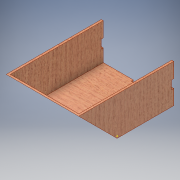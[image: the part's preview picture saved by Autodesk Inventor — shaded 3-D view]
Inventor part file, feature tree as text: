
AUTODESK INVENTOR PART (.ipt)
format: ipt  version: 2017 (Build 210142000, 142)  size: 214,528 bytes
history: native  units: in
note: dims shown in document units (in); Inventor stores cm internally (conversion verified against a paired STEP export)
features: sketch x10, extrude x9, fillet x1
ambient origin geometry x8: Origin, YZ Plane, XZ Plane, XY Plane, X Axis, Y Axis, Z Axis, Center Point
bodies: Solid1 (feature_tree)
feature tree (20):
  extrude  "Extrusion1"  Depth=0.1875in TaperAngle=0.0deg
  sketch  "Sketch2"  dims[d4=0.1875in d5=0.1875in]
  extrude  "Extrusion2"  Depth=0.1875in
  sketch  "Sketch3"  dims[d6=3.3558in d7=0.0in d8=4.7244in]
  sketch  "Sketch4"  dims[d9=45.0deg d11=45.0deg]
  extrude  "Extrusion3"  Depth=3.3558in
  extrude  "Extrusion4"  TaperAngle=45.0deg  [1 undecoded]
  extrude  "Extrusion5"  Depth=3.9557in TaperAngle=0.0deg
  extrude  "Extrusion6"  Depth=3.3558in TaperAngle=0.0deg
  extrude  "Extrusion7"  Depth=6.6929in
  extrude  "Extrusion8"  Depth=2.9528in
  extrude  "Extrusion9"  Depth=0.7874in
  fillet  "Fillet1"  Radius=1.378in
  sketch  "Sketch1"  dims[d0=5.2323in d2=0.1875in d3=0.0in]
  sketch  "Sketch5"  dims[d12=4.1432in d13=0.0in d14=3.9557in d15=0.0in]
  sketch  "Sketch6"  dims[d16=2.5492in d17=0.0in d18=3.3558in d19=0.0in]
  sketch  "Sketch7"  dims[d20=0.1875in d21=0.0in d22=6.6929in]
  sketch  "Sketch8"  dims[d23=2.9528in d24=2.9528in]
  sketch  "Sketch9"  dims[d28=0.1969in d29=0.7874in d30=1.378in]
  sketch  "Sketch10"  dims[d31=1.378in d32=0.1875in d33=0.0in d34=0.7874in d35=0.1969in d36=1.378in d37=1.378in d38=0.1875in d39=0.0in d40=0.0394in d41=0.1969in d42=0.1969in d43=2.9528in d44=0.7874in]
note: 1 required parameter value undecoded (feature->parameter linkage not recoverable at this tier; creation-order binding heuristic only, values carry confidence <= 0.55)
